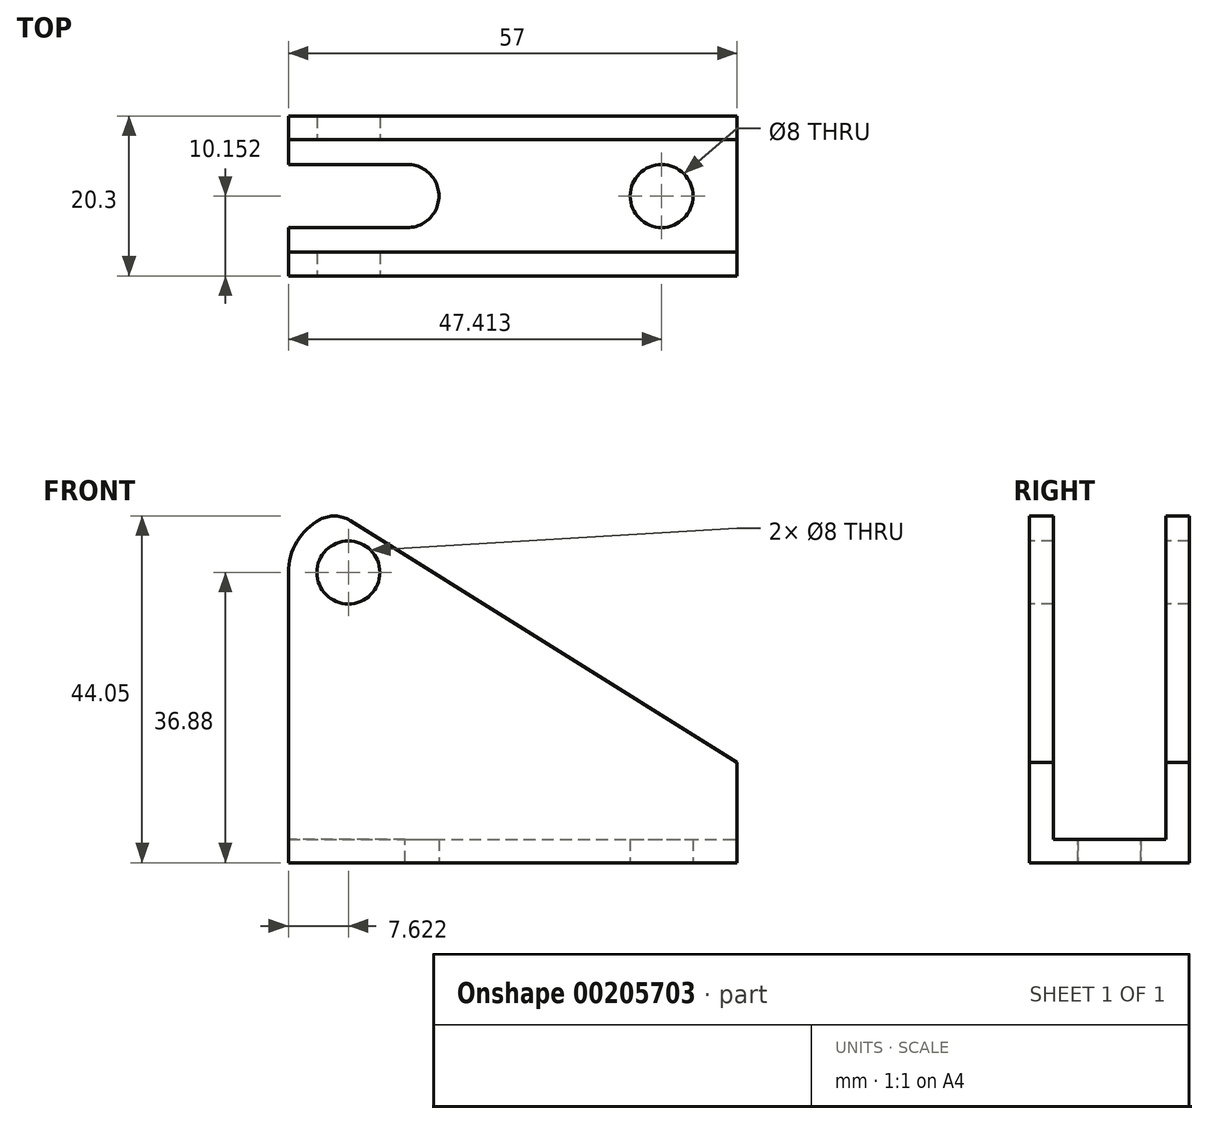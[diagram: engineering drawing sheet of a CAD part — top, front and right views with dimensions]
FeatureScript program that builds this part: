
annotation { "Feature Type Name" : "Feature", "Feature Type Description" : "" }
export const myFeature = defineFeature(function(context is Context, id is Id, definition is map)
    precondition{}
    {
        {
            var Q0;
            Q0=qCreatedBy(makeId("Top.planeOp"),FACE);
            var sketch = newSketch(context, id + "F0", { "sketchPlane" : qUnion([Q0])});
            skLineSegment(sketch, "E0.bottom", {"start": v(-28.43, -5.36) * mm, "end": v(28.57, -5.36) * mm});
            skLineSegment(sketch, "E0.top", {"start": v(-28.43, -25.66) * mm, "end": v(28.57, -25.66) * mm});
            skLineSegment(sketch, "E0.left", {"start": v(-28.43, -5.36) * mm, "end": v(-28.43, -25.66) * mm});
            skLineSegment(sketch, "E0.right", {"start": v(28.57, -5.36) * mm, "end": v(28.57, -25.66) * mm});
            skSolve(sketch);
        }
        {
            var Q0;
            Q0=makeQuery(id+"F0.imprint","IMPRINT",FACE,{"disambiguationData":[TD([[makeQuery(id+"F0.imprint","IMPRINT",EDGE,{"derivedFrom":sQuery(id+"F0.wireOp",EDGE,"E0.bottom")}),-1.0]])]});
            extrude(context, id + "F1", {"entities" : qUnion([Q0]), "depth" : 44.5 * mm});
        }
        {
            var Q0;
            Q0=makeQuery(id+"F1.opExtrude","CAP_FACE",FACE,{"disambiguationData":[OSD([sQuery(id+"F0.wireOp",EDGE,"E0.bottom"),sQuery(id+"F0.wireOp",EDGE,"E0.top"),sQuery(id+"F0.wireOp",EDGE,"E0.left"),sQuery(id+"F0.wireOp",EDGE,"E0.right")])],"isStart":false});
            var sketch = newSketch(context, id + "F2", { "sketchPlane" : qUnion([Q0])});
            skLineSegment(sketch, "E1", {"start": v(-28.43, -25.66) * mm, "end": v(-28.43, -22.66) * mm, "construction": true});
            skLineSegment(sketch, "E2", {"start": v(-28.43, -5.36) * mm, "end": v(-28.43, -8.36) * mm, "construction": true});
            skLineSegment(sketch, "E3", {"start": v(28.57, -25.66) * mm, "end": v(28.57, -22.66) * mm, "construction": true});
            skLineSegment(sketch, "E4", {"start": v(28.57, -5.36) * mm, "end": v(28.57, -8.36) * mm, "construction": true});
            skLineSegment(sketch, "E5.bottom", {"start": v(-28.43, -22.66) * mm, "end": v(28.57, -22.66) * mm});
            skLineSegment(sketch, "E5.top", {"start": v(-28.43, -8.36) * mm, "end": v(28.57, -8.36) * mm});
            skLineSegment(sketch, "E5.left", {"start": v(-28.43, -22.66) * mm, "end": v(-28.43, -8.36) * mm});
            skLineSegment(sketch, "E5.right", {"start": v(28.57, -22.66) * mm, "end": v(28.57, -8.36) * mm});
            skSolve(sketch);
        }
        {
            var Q0;
            Q0 = qSketchRegion(id + "F2", true);
            extrude(context, id + "F3", {"entities" : qUnion([Q0]), "operationType" : NewBodyOperationType.REMOVE, "oppositeDirection" : true, "depth" : 41.5 * mm});
        }
        {
            var Q0;
            {var subQ0=sQuery(id+"F0.wireOp",EDGE,"E0.left");var subQ1=sQuery(id+"F0.wireOp",EDGE,"E0.top");Q0=makeQuery(id+"F3.boolean.opBoolean","SPLIT",EDGE,{"disambiguationData":[TD([makeQuery(id+"F1.opExtrude","SWEPT_FACE",FACE,{"disambiguationData":[OSD([subQ1])]})])],"derivedFrom":makeQuery(id+"F1.opExtrude","CAP_EDGE",EDGE,{"disambiguationData":[OSD([subQ0])],"isStart":false})});}
            var Q1;
            {var subQ0=sQuery(id+"F0.wireOp",EDGE,"E0.bottom");var subQ1=sQuery(id+"F0.wireOp",EDGE,"E0.left");Q1=makeQuery(id+"F3.boolean.opBoolean","SPLIT",EDGE,{"disambiguationData":[TD([makeQuery(id+"F1.opExtrude","SWEPT_FACE",FACE,{"disambiguationData":[OSD([subQ0])]})])],"derivedFrom":makeQuery(id+"F1.opExtrude","CAP_EDGE",EDGE,{"disambiguationData":[OSD([subQ1])],"isStart":false})});}
            fillet(context, id + "F4", {"entities" : qUnion([Q0, Q1]), "radius" : 7.62 * mm, "tangentPropagation" : true, "allowEdgeOverflow" : false});
        }
        {
            var Q0;
            {var subQ0=sQuery(id+"F0.wireOp",EDGE,"E0.right");var subQ1=sQuery(id+"F0.wireOp",EDGE,"E0.top");Q0=makeQuery(id+"F3.boolean.opBoolean","SPLIT",EDGE,{"disambiguationData":[TD([makeQuery(id+"F1.opExtrude","SWEPT_FACE",FACE,{"disambiguationData":[OSD([subQ1])]})])],"derivedFrom":makeQuery(id+"F1.opExtrude","CAP_EDGE",EDGE,{"disambiguationData":[OSD([subQ0])],"isStart":false})});}
            chamfer(context, id + "F5", {"entities" : qUnion([Q0]), "chamferType" : ChamferType.OFFSET_ANGLE, "width" : 31.75 * mm, "oppositeDirection" : false, "angle" : 58 * degree});
        }
        {
            var Q0;
            {var subQ0=sQuery(id+"F0.wireOp",EDGE,"E0.bottom");var subQ1=sQuery(id+"F0.wireOp",EDGE,"E0.right");Q0=makeQuery(id+"F3.boolean.opBoolean","SPLIT",EDGE,{"disambiguationData":[TD([makeQuery(id+"F1.opExtrude","SWEPT_FACE",FACE,{"disambiguationData":[OSD([subQ0])]})])],"derivedFrom":makeQuery(id+"F1.opExtrude","CAP_EDGE",EDGE,{"disambiguationData":[OSD([subQ1])],"isStart":false})});}
            chamfer(context, id + "F6", {"entities" : qUnion([Q0]), "chamferType" : ChamferType.OFFSET_ANGLE, "width" : 31.75 * mm, "oppositeDirection" : false, "angle" : 58 * degree, "tangentPropagation" : true});
        }
        {
            var Q0;
            Q0=makeQuery(id+"F1.opExtrude","SWEPT_FACE",FACE,{"disambiguationData":[OSD([sQuery(id+"F0.wireOp",EDGE,"E0.top")])]});
            var sketch = newSketch(context, id + "F7", { "sketchPlane" : qUnion([Q0])});
            skCircle(sketch, "E6", {"center": v(-20.8, 36.88) * mm, "radius": 4 * mm});
            skSolve(sketch);
        }
        {
            var Q0;
            Q0=makeQuery(id+"F7.imprint","IMPRINT",FACE,{"disambiguationData":[TD([[makeQuery(id+"F7.imprint","IMPRINT",EDGE,{"derivedFrom":sQuery(id+"F7.wireOp",EDGE,"E6")}),1.0]])]});
            extrude(context, id + "F8", {"entities" : qUnion([Q0]), "operationType" : NewBodyOperationType.REMOVE, "oppositeDirection" : true, "depth" : 25.4 * mm});
        }
        {
            var Q0;
            Q0=makeQuery(id+"F3.boolean.opBoolean","COPY",FACE,{"derivedFrom":makeQuery(id+"F3.opExtrude","CAP_FACE",FACE,{"disambiguationData":[OSD([sQuery(id+"F2.wireOp",EDGE,"E5.bottom"),sQuery(id+"F2.wireOp",EDGE,"E5.top"),sQuery(id+"F2.wireOp",EDGE,"E5.left"),sQuery(id+"F2.wireOp",EDGE,"E5.right")])],"isStart":false})});
            var sketch = newSketch(context, id + "F9", { "sketchPlane" : qUnion([Q0])});
            skPoint(sketch, "E7", {"position": v(18.98, -15.5) * mm});
            skPoint(sketch, "E7.positionSnap0", {"position": v(28.57, -15.5) * mm});
            skSolve(sketch);
        }
        {
            var Q0;
            Q0=sQuery(id+"F9.wireOp",VERTEX,"E7");
            var Q1;
            Q1=makeQuery(id+"F1.opExtrude","SWEPT_BODY",BODY,{"disambiguationData":[OSD([sQuery(id+"F0.wireOp",EDGE,"E0.bottom"),sQuery(id+"F0.wireOp",EDGE,"E0.top"),sQuery(id+"F0.wireOp",EDGE,"E0.left"),sQuery(id+"F0.wireOp",EDGE,"E0.right")])]});
            hole(context, id + "F10", {"style" : HoleStyle.SIMPLE, "endStyle" : HoleEndStyle.THROUGH, "holeDiameter" : 8 * mm, "locations" : qUnion([Q0]), "scope" : qUnion([Q1]), "isTappedThrough" : true});
        }
        {
            var Q0;
            Q0=makeQuery(id+"F3.boolean.opBoolean","COPY",FACE,{"derivedFrom":makeQuery(id+"F3.opExtrude","CAP_FACE",FACE,{"disambiguationData":[OSD([sQuery(id+"F2.wireOp",EDGE,"E5.bottom"),sQuery(id+"F2.wireOp",EDGE,"E5.top"),sQuery(id+"F2.wireOp",EDGE,"E5.left"),sQuery(id+"F2.wireOp",EDGE,"E5.right")])],"isStart":false})});
            var sketch = newSketch(context, id + "F11", { "sketchPlane" : qUnion([Q0])});
            skPoint(sketch, "E8", {"position": v(-13.3, -15.5) * mm});
            skPoint(sketch, "E8.positionSnap0", {"position": v(-28.43, -15.5) * mm});
            skSolve(sketch);
        }
        {
            var Q0;
            Q0=sQuery(id+"F11.wireOp",VERTEX,"E8");
            var Q1;
            Q1=makeQuery(id+"F1.opExtrude","SWEPT_BODY",BODY,{"disambiguationData":[OSD([sQuery(id+"F0.wireOp",EDGE,"E0.bottom"),sQuery(id+"F0.wireOp",EDGE,"E0.top"),sQuery(id+"F0.wireOp",EDGE,"E0.left"),sQuery(id+"F0.wireOp",EDGE,"E0.right")])]});
            hole(context, id + "F12", {"style" : HoleStyle.SIMPLE, "endStyle" : HoleEndStyle.THROUGH, "holeDiameter" : 8 * mm, "locations" : qUnion([Q0]), "scope" : qUnion([Q1]), "isTappedThrough" : true});
        }
        {
            var Q0;
            Q0=makeQuery(id+"F3.boolean.opBoolean","COPY",FACE,{"derivedFrom":makeQuery(id+"F3.opExtrude","CAP_FACE",FACE,{"disambiguationData":[OSD([sQuery(id+"F2.wireOp",EDGE,"E5.bottom"),sQuery(id+"F2.wireOp",EDGE,"E5.top"),sQuery(id+"F2.wireOp",EDGE,"E5.left"),sQuery(id+"F2.wireOp",EDGE,"E5.right")])],"isStart":false})});
            var sketch = newSketch(context, id + "F13", { "sketchPlane" : qUnion([Q0])});
            skLineSegment(sketch, "E9.bottom", {"start": v(-13.6, -19.5) * mm, "end": v(-28.43, -19.5) * mm});
            skLineSegment(sketch, "E9.top", {"start": v(-13.6, -11.5) * mm, "end": v(-28.43, -11.5) * mm});
            skLineSegment(sketch, "E9.left", {"start": v(-13.6, -19.5) * mm, "end": v(-13.6, -11.5) * mm});
            skLineSegment(sketch, "E9.right", {"start": v(-28.43, -19.5) * mm, "end": v(-28.43, -11.5) * mm});
            skSolve(sketch);
        }
        {
            var Q0;
            {var subQ4=sQuery(id+"F13.wireOp",EDGE,"E9.bottom");Q0=makeQuery(id+"F13.imprint","IMPRINT",FACE,{"disambiguationData":[TD([[makeQuery(id+"F13.imprint","IMPRINT",EDGE,{"derivedFrom":subQ4}),-1.0]])]});}
            extrude(context, id + "F14", {"entities" : qUnion([Q0]), "operationType" : NewBodyOperationType.REMOVE, "oppositeDirection" : true, "depth" : 25.4 * mm});
        }
        {
            var Q0;
            {var subQ0=sQuery(id+"F0.wireOp",EDGE,"E0.right");var subQ1=sQuery(id+"F0.wireOp",EDGE,"E0.left");var subQ2=sQuery(id+"F0.wireOp",EDGE,"E0.top");var subQ4=makeQuery(id+"F1.opExtrude","SWEPT_FACE",FACE,{"disambiguationData":[OSD([subQ2])]});Q0=makeQuery(id+"F5.opChamfer","BLEND_EDGE",EDGE,{"blendedFrom":[makeQuery(id+"F3.boolean.opBoolean","SPLIT",EDGE,{"disambiguationData":[TD([subQ4])],"derivedFrom":makeQuery(id+"F1.opExtrude","CAP_EDGE",EDGE,{"disambiguationData":[OSD([subQ0])],"isStart":false})}),makeQuery(id+"F4.opFillet","BLEND_FACE",FACE,{"disambiguationData":[OSD([subQ1]),TDD([makeQuery(id+"F3.boolean.opBoolean","SPLIT",EDGE,{"disambiguationData":[TD([subQ4])],"derivedFrom":makeQuery(id+"F1.opExtrude","CAP_EDGE",EDGE,{"disambiguationData":[OSD([subQ1])],"isStart":false})})])]})],"blendedInto":[makeQuery(id+"F4.opFillet","BLEND_FACE",FACE,{"disambiguationData":[OSD([subQ1]),TDD([makeQuery(id+"F3.boolean.opBoolean","SPLIT",EDGE,{"disambiguationData":[TD([subQ4])],"derivedFrom":makeQuery(id+"F1.opExtrude","CAP_EDGE",EDGE,{"disambiguationData":[OSD([subQ1])],"isStart":false})})])]})]});}
            var Q1;
            {var subQ0=sQuery(id+"F0.wireOp",EDGE,"E0.bottom");var subQ1=makeQuery(id+"F1.opExtrude","SWEPT_FACE",FACE,{"disambiguationData":[OSD([subQ0])]});var subQ3=sQuery(id+"F0.wireOp",EDGE,"E0.right");var subQ4=sQuery(id+"F0.wireOp",EDGE,"E0.left");Q1=makeQuery(id+"F6.opChamfer","BLEND_EDGE",EDGE,{"blendedFrom":[makeQuery(id+"F3.boolean.opBoolean","SPLIT",EDGE,{"disambiguationData":[TD([subQ1])],"derivedFrom":makeQuery(id+"F1.opExtrude","CAP_EDGE",EDGE,{"disambiguationData":[OSD([subQ3])],"isStart":false})}),makeQuery(id+"F4.opFillet","BLEND_FACE",FACE,{"disambiguationData":[OSD([subQ4]),TDD([makeQuery(id+"F3.boolean.opBoolean","SPLIT",EDGE,{"disambiguationData":[TD([subQ1])],"derivedFrom":makeQuery(id+"F1.opExtrude","CAP_EDGE",EDGE,{"disambiguationData":[OSD([subQ4])],"isStart":false})})])]})],"blendedInto":[makeQuery(id+"F4.opFillet","BLEND_FACE",FACE,{"disambiguationData":[OSD([subQ4]),TDD([makeQuery(id+"F3.boolean.opBoolean","SPLIT",EDGE,{"disambiguationData":[TD([subQ1])],"derivedFrom":makeQuery(id+"F1.opExtrude","CAP_EDGE",EDGE,{"disambiguationData":[OSD([subQ4])],"isStart":false})})])]})]});}
            fillet(context, id + "F15", {"entities" : qUnion([Q0, Q1]), "radius" : 3.8 * mm, "tangentPropagation" : true, "allowEdgeOverflow" : false});
        }
    });
